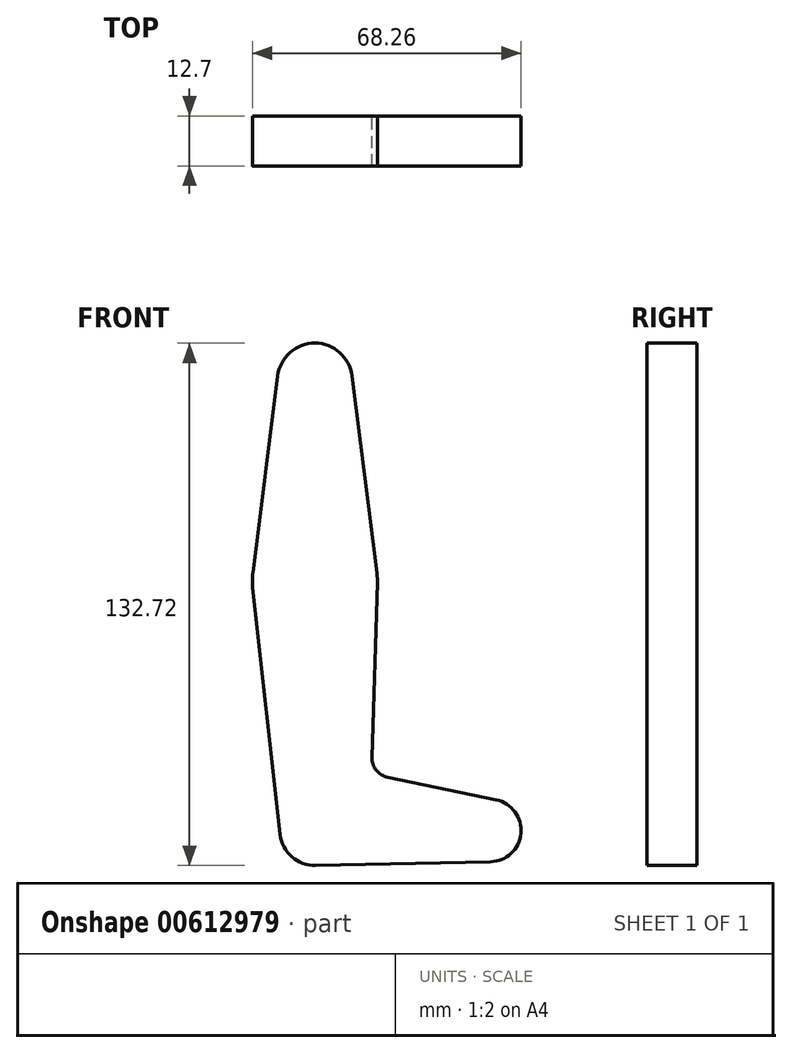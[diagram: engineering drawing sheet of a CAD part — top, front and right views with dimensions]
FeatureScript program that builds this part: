
annotation { "Feature Type Name" : "Feature", "Feature Type Description" : "" }
export const myFeature = defineFeature(function(context is Context, id is Id, definition is map)
    precondition{}
    {
        {
            var Q0;
            Q0=qCreatedBy(makeId("Front.planeOp"),FACE);
            var sketch = newSketch(context, id + "F0", { "sketchPlane" : qUnion([Q0])});
            skLineSegment(sketch, "E0", {"start": v(0, 0) * mm, "end": v(44.45, 0) * mm, "construction": true});
            skLineSegment(sketch, "E1", {"start": v(0, 0) * mm, "end": v(0, 63.5) * mm, "construction": true});
            skLineSegment(sketch, "E2", {"start": v(0, 63.5) * mm, "end": v(0, 114.3) * mm, "construction": true});
            skCircle(sketch, "E3", {"center": v(0, 114.3) * mm, "radius": 9.53 * mm});
            skCircle(sketch, "E4", {"center": v(0, 63.5) * mm, "radius": 15.88 * mm});
            skCircle(sketch, "E5", {"center": v(44.45, 0) * mm, "radius": 7.94 * mm});
            skCircle(sketch, "E6", {"center": v(0, 0) * mm, "radius": 8.9 * mm});
            skLineSegment(sketch, "E7", {"start": v(-9.45, 115.5) * mm, "end": v(-15.75, 65.48) * mm});
            skLineSegment(sketch, "E8", {"start": v(9.45, 115.5) * mm, "end": v(15.75, 65.48) * mm});
            skLineSegment(sketch, "E9", {"start": v(-15.78, 61.75) * mm, "end": v(-8.84, -0.98) * mm});
            skLineSegment(sketch, "E10", {"start": v(15.87, 63.01) * mm, "end": v(14.5, 18.63) * mm});
            skLineSegment(sketch, "E11", {"start": v(18.54, 13.5) * mm, "end": v(46.07, 7.77) * mm});
            skLineSegment(sketch, "E12", {"start": v(0.2, -8.89) * mm, "end": v(44.62, -7.94) * mm});
            skLineSegment(sketch, "E13", {"start": v(0, 0) * mm, "end": v(14.37, 14.37) * mm, "construction": true});
            skPoint(sketch, "E14.visualSharp", {"position": v(14.37, 14.37) * mm});
            skArc(sketch, "E14.filletArc", {"start": v(14.5, 18.63) * mm, "mid": v(15.59, 15.33) * mm, "end": v(18.54, 13.5) * mm});
            skSolve(sketch);
        }
        {
            var Q0;
            Q0=qCreatedBy(makeId("Front.planeOp"),FACE);
            var sketch = newSketch(context, id + "F1", { "sketchPlane" : qUnion([Q0])});
            skLineSegment(sketch, "E15", {"start": v(-71.3, 42.56) * mm, "end": v(-25.4, 144.5) * mm});
            skSolve(sketch);
        }
        {
            var Q0;
            Q0 = qSketchRegion(id + "F0", true);
            extrude(context, id + "F2", {"entities" : qUnion([Q0]), "depth" : 12.7 * mm, "offsetDistance" : 25.4 * mm});
        }
    });
